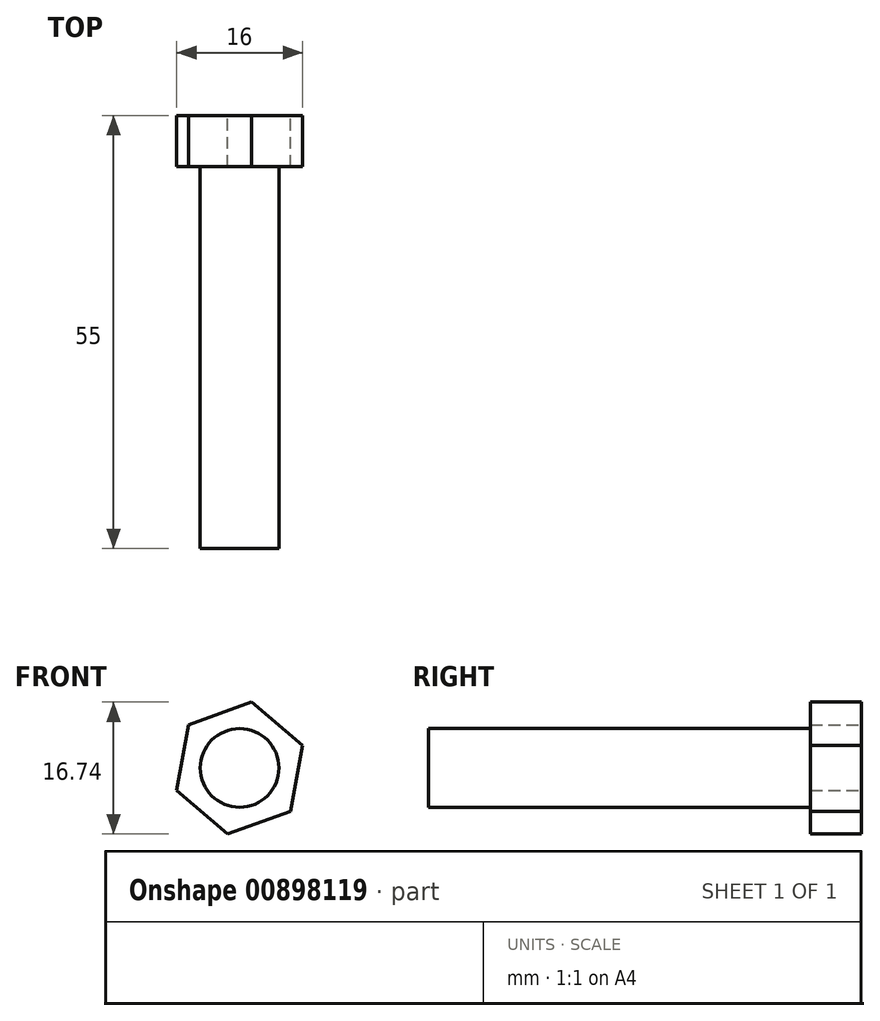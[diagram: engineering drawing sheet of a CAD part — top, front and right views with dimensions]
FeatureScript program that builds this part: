
annotation { "Feature Type Name" : "Feature", "Feature Type Description" : "" }
export const myFeature = defineFeature(function(context is Context, id is Id, definition is map)
    precondition{}
    {
        {
            var Q0;
            Q0=qCreatedBy(makeId("Front.planeOp"),FACE);
            var sketch = newSketch(context, id + "F0", { "sketchPlane" : qUnion([Q0])});
            skCircle(sketch, "E0", {"center": v(0, 0) * mm, "radius": 8.5 * mm});
            skCircle(sketch, "E1.cCircle", {"center": v(0, 0) * mm, "radius": 8.5 * mm, "construction": true});
            skLineSegment(sketch, "E1.0", {"start": v(-6.5, 5.49) * mm, "end": v(1.5, 8.37) * mm});
            skLineSegment(sketch, "E1.1", {"start": v(1.5, 8.37) * mm, "end": v(8, 2.88) * mm});
            skLineSegment(sketch, "E1.2", {"start": v(8, 2.88) * mm, "end": v(6.5, -5.49) * mm});
            skLineSegment(sketch, "E1.3", {"start": v(6.5, -5.49) * mm, "end": v(-1.5, -8.37) * mm});
            skLineSegment(sketch, "E1.4", {"start": v(-1.5, -8.37) * mm, "end": v(-8, -2.88) * mm});
            skLineSegment(sketch, "E1.5", {"start": v(-8, -2.88) * mm, "end": v(-6.5, 5.49) * mm});
            skCircle(sketch, "E2", {"center": v(0, 0) * mm, "radius": 5 * mm});
            skSolve(sketch);
        }
        {
            var Q0;
            Q0=makeQuery(id+"F0.imprint","IMPRINT",FACE,{"disambiguationData":[TD([[makeQuery(id+"F0.imprint","IMPRINT",EDGE,{"derivedFrom":sQuery(id+"F0.wireOp",EDGE,"E1.0")}),-1.0]])]});
            extrude(context, id + "F1", {"entities" : qUnion([Q0]), "depth" : 6.5 * mm, "offsetDistance" : 25 * mm});
        }
        {
            var Q0;
            Q0=makeQuery(id+"F0.imprint","IMPRINT",FACE,{"disambiguationData":[TD([[makeQuery(id+"F0.imprint","IMPRINT",EDGE,{"derivedFrom":sQuery(id+"F0.wireOp",EDGE,"E2")}),1.0]])]});
            extrude(context, id + "F2", {"entities" : qUnion([Q0]), "operationType" : NewBodyOperationType.ADD, "depth" : 55 * mm, "offsetDistance" : 25 * mm});
        }
    });
